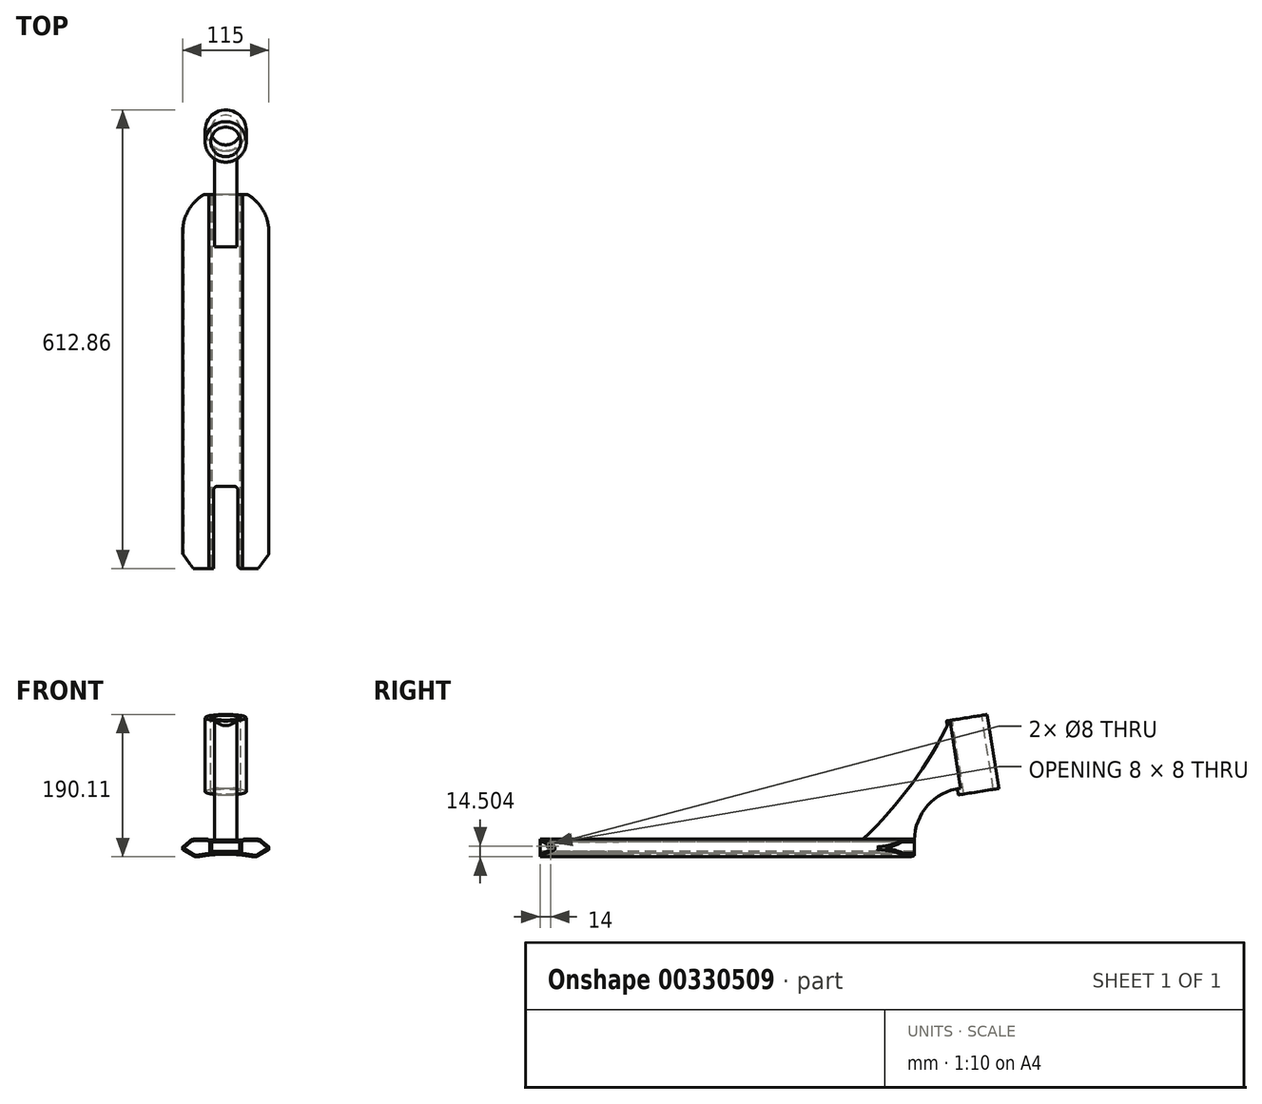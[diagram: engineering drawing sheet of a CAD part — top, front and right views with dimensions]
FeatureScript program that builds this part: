
annotation { "Feature Type Name" : "Feature", "Feature Type Description" : "" }
export const myFeature = defineFeature(function(context is Context, id is Id, definition is map)
    precondition{}
    {
        {
            var Q0;
            Q0=qCreatedBy(makeId("Front.planeOp"),FACE);
            var sketch = newSketch(context, id + "F0", { "sketchPlane" : qUnion([Q0])});
            skLineSegment(sketch, "E0", {"start": v(0, 0) * mm, "end": v(0, 27.74) * mm, "construction": true});
            skLineSegment(sketch, "E1", {"start": v(0, 23.15) * mm, "end": v(22.5, 23.15) * mm});
            skLineSegment(sketch, "E2", {"start": v(22.5, 23.15) * mm, "end": v(22.5, 24.45) * mm});
            skLineSegment(sketch, "E3", {"start": v(22.5, 24.45) * mm, "end": v(45.58, 24.45) * mm});
            skLineSegment(sketch, "E4", {"start": v(45.58, 24.45) * mm, "end": v(57.5, 14.45) * mm});
            skLineSegment(sketch, "E5", {"start": v(57.5, 14.45) * mm, "end": v(57.5, 10.45) * mm});
            skLineSegment(sketch, "E6", {"start": v(57.5, 10.45) * mm, "end": v(40.18, 0.45) * mm});
            skLineSegment(sketch, "E7.MirrorCS", {"start": v(0, 23.15) * mm, "end": v(-22.5, 23.15) * mm});
            skLineSegment(sketch, "E8.MirrorCS", {"start": v(-22.5, 23.15) * mm, "end": v(-22.5, 24.45) * mm});
            skLineSegment(sketch, "E9.MirrorCS", {"start": v(-22.5, 24.45) * mm, "end": v(-45.58, 24.45) * mm});
            skLineSegment(sketch, "E10.MirrorCS", {"start": v(-45.58, 24.45) * mm, "end": v(-57.5, 14.45) * mm});
            skLineSegment(sketch, "E11.MirrorCS", {"start": v(-57.5, 14.45) * mm, "end": v(-57.5, 10.45) * mm});
            skLineSegment(sketch, "E12.MirrorCS", {"start": v(-57.5, 10.45) * mm, "end": v(-40.18, 0.45) * mm});
            skArc(sketch, "E13", {"start": v(40.18, 0.45) * mm, "mid": v(0, 4.53) * mm, "end": v(-40.18, 0.45) * mm});
            skSolve(sketch);
        }
        {
            var Q0;
            Q0 = qSketchRegion(id + "F0", true);
            extrude(context, id + "F1", {"entities" : qUnion([Q0]), "endBound" : BoundingType.SYMMETRIC, "depth" : 500 * mm});
        }
        {
            var Q0;
            Q0=qCreatedBy(makeId("Front.planeOp"),FACE);
            var sketch = newSketch(context, id + "F2", { "sketchPlane" : qUnion([Q0])});
            skLineSegment(sketch, "E14.bottom", {"start": v(-19, 21.15) * mm, "end": v(19, 21.15) * mm});
            skLineSegment(sketch, "E14.top", {"start": v(-19, 8.15) * mm, "end": v(19, 8.15) * mm});
            skLineSegment(sketch, "E14.left", {"start": v(-19, 21.15) * mm, "end": v(-19, 8.15) * mm});
            skLineSegment(sketch, "E14.right", {"start": v(19, 21.15) * mm, "end": v(19, 8.15) * mm});
            skSolve(sketch);
        }
        {
            var Q0;
            Q0 = qSketchRegion(id + "F2", true);
            extrude(context, id + "F3", {"entities" : qUnion([Q0]), "operationType" : NewBodyOperationType.REMOVE, "endBound" : BoundingType.SYMMETRIC, "oppositeDirection" : true, "depth" : 500 * mm});
        }
        {
            var Q0;
            Q0=makeQuery(id+"F1.opExtrude","SWEPT_EDGE",EDGE,{"disambiguationData":[OSD([sQuery(id+"F0.wireOp",EDGE,"E8.MirrorCS"),sQuery(id+"F0.wireOp",EDGE,"E9.MirrorCS")])]});
            var Q1;
            Q1=makeQuery(id+"F1.opExtrude","SWEPT_EDGE",EDGE,{"disambiguationData":[OSD([sQuery(id+"F0.wireOp",EDGE,"E2"),sQuery(id+"F0.wireOp",EDGE,"E3")])]});
            fillet(context, id + "F4", {"entities" : qUnion([Q0, Q1]), "radius" : 2 * mm, "tangentPropagation" : true, "allowEdgeOverflow" : false});
        }
        {
            var Q0;
            Q0=makeQuery(id+"F1.opExtrude","SWEPT_EDGE",EDGE,{"disambiguationData":[OSD([sQuery(id+"F0.wireOp",EDGE,"E9.MirrorCS"),sQuery(id+"F0.wireOp",EDGE,"E10.MirrorCS")])]});
            var Q1;
            Q1=makeQuery(id+"F1.opExtrude","SWEPT_EDGE",EDGE,{"disambiguationData":[OSD([sQuery(id+"F0.wireOp",EDGE,"E12.MirrorCS"),sQuery(id+"F0.wireOp",EDGE,"E13")])]});
            var Q2;
            Q2=makeQuery(id+"F1.opExtrude","SWEPT_EDGE",EDGE,{"disambiguationData":[OSD([sQuery(id+"F0.wireOp",EDGE,"E6"),sQuery(id+"F0.wireOp",EDGE,"E13")])]});
            var Q3;
            Q3=makeQuery(id+"F1.opExtrude","SWEPT_EDGE",EDGE,{"disambiguationData":[OSD([sQuery(id+"F0.wireOp",EDGE,"E3"),sQuery(id+"F0.wireOp",EDGE,"E4")])]});
            fillet(context, id + "F5", {"entities" : qUnion([Q0, Q1, Q2, Q3]), "radius" : 9 * mm, "tangentPropagation" : true, "allowEdgeOverflow" : false});
        }
        {
            var Q0;
            Q0=makeQuery(id+"F1.opExtrude","SWEPT_EDGE",EDGE,{"disambiguationData":[OSD([sQuery(id+"F0.wireOp",EDGE,"E4"),sQuery(id+"F0.wireOp",EDGE,"E5")])]});
            var Q1;
            Q1=makeQuery(id+"F1.opExtrude","SWEPT_EDGE",EDGE,{"disambiguationData":[OSD([sQuery(id+"F0.wireOp",EDGE,"E5"),sQuery(id+"F0.wireOp",EDGE,"E6")])]});
            var Q2;
            Q2=makeQuery(id+"F1.opExtrude","SWEPT_EDGE",EDGE,{"disambiguationData":[OSD([sQuery(id+"F0.wireOp",EDGE,"E11.MirrorCS"),sQuery(id+"F0.wireOp",EDGE,"E12.MirrorCS")])]});
            var Q3;
            Q3=makeQuery(id+"F1.opExtrude","SWEPT_EDGE",EDGE,{"disambiguationData":[OSD([sQuery(id+"F0.wireOp",EDGE,"E10.MirrorCS"),sQuery(id+"F0.wireOp",EDGE,"E11.MirrorCS")])]});
            fillet(context, id + "F6", {"entities" : qUnion([Q0, Q1, Q2, Q3]), "radius" : 1 * mm, "tangentPropagation" : true, "allowEdgeOverflow" : false});
        }
        {
            var Q0;
            Q0=makeQuery(id+"F1.opExtrude","CAP_FACE",FACE,{"disambiguationData":[OSD([sQuery(id+"F0.wireOp",EDGE,"E1"),sQuery(id+"F0.wireOp",EDGE,"E2"),sQuery(id+"F0.wireOp",EDGE,"E3"),sQuery(id+"F0.wireOp",EDGE,"E4"),sQuery(id+"F0.wireOp",EDGE,"E5"),sQuery(id+"F0.wireOp",EDGE,"E6"),sQuery(id+"F0.wireOp",EDGE,"E7.MirrorCS"),sQuery(id+"F0.wireOp",EDGE,"E8.MirrorCS"),sQuery(id+"F0.wireOp",EDGE,"E9.MirrorCS"),sQuery(id+"F0.wireOp",EDGE,"E10.MirrorCS"),sQuery(id+"F0.wireOp",EDGE,"E11.MirrorCS"),sQuery(id+"F0.wireOp",EDGE,"E12.MirrorCS"),sQuery(id+"F0.wireOp",EDGE,"E13")])],"isStart":false});
            var sketch = newSketch(context, id + "F7", { "sketchPlane" : qUnion([Q0])});
            skLineSegment(sketch, "E15.0.0", {"start": v(43.1, 2.14) * mm, "end": v(57, 10.16) * mm});
            skArc(sketch, "E15.0.1", {"start": v(57, 10.16) * mm, "mid": v(57.37, 10.53) * mm, "end": v(57.5, 11.03) * mm});
            skLineSegment(sketch, "E15.0.2", {"start": v(57.5, 11.03) * mm, "end": v(57.5, 13.99) * mm});
            skArc(sketch, "E15.0.3", {"start": v(57.5, 13.99) * mm, "mid": v(57.4, 14.4) * mm, "end": v(57.14, 14.75) * mm});
            skLineSegment(sketch, "E15.0.4", {"start": v(57.14, 14.75) * mm, "end": v(48.1, 22.35) * mm});
            skArc(sketch, "E15.0.5", {"start": v(48.1, 22.35) * mm, "mid": v(45.38, 23.9) * mm, "end": v(42.3, 24.45) * mm});
            skLineSegment(sketch, "E15.0.6", {"start": v(42.3, 24.45) * mm, "end": v(24.37, 24.45) * mm});
            skArc(sketch, "E15.0.7", {"start": v(24.37, 24.45) * mm, "mid": v(23.23, 24.1) * mm, "end": v(22.5, 23.15) * mm});
            skLineSegment(sketch, "E15.0.8", {"start": v(22.5, 23.15) * mm, "end": v(-22.5, 23.15) * mm});
            skArc(sketch, "E15.0.9", {"start": v(-22.5, 23.15) * mm, "mid": v(-23.23, 24.1) * mm, "end": v(-24.37, 24.45) * mm});
            skLineSegment(sketch, "E15.0.10", {"start": v(-24.37, 24.45) * mm, "end": v(-42.3, 24.45) * mm});
            skArc(sketch, "E15.0.11", {"start": v(-42.3, 24.45) * mm, "mid": v(-45.38, 23.9) * mm, "end": v(-48.1, 22.35) * mm});
            skLineSegment(sketch, "E15.0.12", {"start": v(-48.1, 22.35) * mm, "end": v(-57.14, 14.75) * mm});
            skArc(sketch, "E15.0.13", {"start": v(-57.14, 14.75) * mm, "mid": v(-57.4, 14.4) * mm, "end": v(-57.5, 13.99) * mm});
            skLineSegment(sketch, "E15.0.14", {"start": v(-57.5, 13.99) * mm, "end": v(-57.5, 11.03) * mm});
            skArc(sketch, "E15.0.15", {"start": v(-57.5, 11.03) * mm, "mid": v(-57.37, 10.53) * mm, "end": v(-57, 10.16) * mm});
            skLineSegment(sketch, "E15.0.16", {"start": v(-57, 10.16) * mm, "end": v(-43.1, 2.14) * mm});
            skArc(sketch, "E15.0.17", {"start": v(-43.1, 2.14) * mm, "mid": v(-40.12, 1.06) * mm, "end": v(-36.94, 1.09) * mm});
            skArc(sketch, "E15.0.18", {"start": v(-36.94, 1.09) * mm, "mid": v(0, 4.53) * mm, "end": v(36.94, 1.09) * mm});
            skArc(sketch, "E15.0.19", {"start": v(36.94, 1.09) * mm, "mid": v(40.12, 1.06) * mm, "end": v(43.1, 2.14) * mm});
            skArc(sketch, "E16.0", {"start": v(-37.3, 3.05) * mm, "mid": v(0, 6.53) * mm, "end": v(37.3, 3.05) * mm});
            skArc(sketch, "E16.1", {"start": v(-42.1, 3.87) * mm, "mid": v(-39.78, 3.03) * mm, "end": v(-37.3, 3.05) * mm});
            skLineSegment(sketch, "E16.2", {"start": v(-24.37, 22.45) * mm, "end": v(-42.3, 22.45) * mm});
            skArc(sketch, "E16.3", {"start": v(-42.3, 22.45) * mm, "mid": v(-44.7, 22.03) * mm, "end": v(-46.8, 20.81) * mm});
            skLineSegment(sketch, "E16.4", {"start": v(-46.8, 20.81) * mm, "end": v(-55.76, 13.3) * mm});
            skLineSegment(sketch, "E16.5", {"start": v(-55.61, 11.67) * mm, "end": v(-42.1, 3.87) * mm});
            skPoint(sketch, "E17.visualSharp", {"position": v(-56.85, 12.39) * mm});
            skArc(sketch, "E17.filletArc", {"start": v(-55.76, 13.3) * mm, "mid": v(-56.1, 12.45) * mm, "end": v(-55.61, 11.67) * mm});
            skLineSegment(sketch, "E18", {"start": v(-21, 5.43) * mm, "end": v(-21, 21.15) * mm});
            skLineSegment(sketch, "E19", {"start": v(-21, 21.15) * mm, "end": v(-22.5, 21.15) * mm});
            skArc(sketch, "E20", {"start": v(-22.5, 21.15) * mm, "mid": v(-23.23, 22.1) * mm, "end": v(-24.37, 22.45) * mm});
            skLineSegment(sketch, "E21.MirrorCS", {"start": v(21, 5.43) * mm, "end": v(21, 21.15) * mm});
            skLineSegment(sketch, "E22.MirrorCS", {"start": v(21, 21.15) * mm, "end": v(22.5, 21.15) * mm});
            skArc(sketch, "E23.MirrorCS", {"start": v(22.5, 21.15) * mm, "mid": v(23.23, 22.1) * mm, "end": v(24.37, 22.45) * mm});
            skLineSegment(sketch, "E24.MirrorCS", {"start": v(24.37, 22.45) * mm, "end": v(42.3, 22.45) * mm});
            skArc(sketch, "E25.MirrorCS", {"start": v(42.3, 22.45) * mm, "mid": v(44.7, 22.03) * mm, "end": v(46.8, 20.81) * mm});
            skLineSegment(sketch, "E26.MirrorCS", {"start": v(46.8, 20.81) * mm, "end": v(55.76, 13.3) * mm});
            skArc(sketch, "E27.MirrorCS", {"start": v(55.76, 13.3) * mm, "mid": v(56.1, 12.45) * mm, "end": v(55.61, 11.67) * mm});
            skLineSegment(sketch, "E28.MirrorCS", {"start": v(55.61, 11.67) * mm, "end": v(42.1, 3.87) * mm});
            skArc(sketch, "E29.MirrorCS", {"start": v(42.1, 3.87) * mm, "mid": v(39.78, 3.03) * mm, "end": v(37.3, 3.05) * mm});
            skArc(sketch, "E30.MirrorCS", {"start": v(37.3, 3.05) * mm, "mid": v(0, 6.53) * mm, "end": v(-37.3, 3.05) * mm});
            skSolve(sketch);
        }
        {
            var Q0;
            {var subQ0=sQuery(id+"F7.wireOp",EDGE,"E16.1");Q0=makeQuery(id+"F7.imprint","IMPRINT",FACE,{"disambiguationData":[TD([[makeQuery(id+"F7.imprint","IMPRINT",EDGE,{"derivedFrom":subQ0}),1.0]])]});}
            var Q1;
            {var subQ0=sQuery(id+"F7.wireOp",EDGE,"E21.MirrorCS");Q1=makeQuery(id+"F7.imprint","IMPRINT",FACE,{"disambiguationData":[TD([[makeQuery(id+"F7.imprint","IMPRINT",EDGE,{"derivedFrom":subQ0}),-1.0]])]});}
            extrude(context, id + "F8", {"entities" : qUnion([Q0, Q1]), "operationType" : NewBodyOperationType.REMOVE, "endBound" : BoundingType.THROUGH_ALL, "oppositeDirection" : true, "depth" : 25 * mm});
        }
        {
            var Q0;
            Q0=qCreatedBy(makeId("Top.planeOp"),FACE);
            var sketch = newSketch(context, id + "F9", { "sketchPlane" : qUnion([Q0])});
            skArc(sketch, "E31", {"start": v(57.5, 200) * mm, "mid": v(0, 257.5) * mm, "end": v(-57.5, 200) * mm});
            skLineSegment(sketch, "E32", {"start": v(57.5, 200) * mm, "end": v(57.5, 280) * mm});
            skLineSegment(sketch, "E33", {"start": v(57.5, 280) * mm, "end": v(-57.5, 280) * mm});
            skLineSegment(sketch, "E34", {"start": v(-57.5, 280) * mm, "end": v(-57.5, 200) * mm});
            skSolve(sketch);
        }
        {
            var Q0;
            Q0 = qSketchRegion(id + "F9", true);
            extrude(context, id + "F10", {"entities" : qUnion([Q0]), "operationType" : NewBodyOperationType.REMOVE, "endBound" : BoundingType.THROUGH_ALL, "depth" : 25 * mm, "hasSecondDirection" : true, "secondDirectionBound" : SecondDirectionBoundingType.THROUGH_ALL, "secondDirectionOppositeDirection" : true, "secondDirectionDepth" : 25 * mm});
        }
        {
            var Q0;
            Q0=qCreatedBy(makeId("Top.planeOp"),FACE);
            var sketch = newSketch(context, id + "F11", { "sketchPlane" : qUnion([Q0])});
            skLineSegment(sketch, "E35", {"start": v(-68, -216) * mm, "end": v(-43.3, -250) * mm});
            skLineSegment(sketch, "E36", {"start": v(-68, -216) * mm, "end": v(-68, -346) * mm});
            skLineSegment(sketch, "E37", {"start": v(-68, -346) * mm, "end": v(68, -346) * mm});
            skLineSegment(sketch, "E38", {"start": v(68, -346) * mm, "end": v(68, -216) * mm});
            skLineSegment(sketch, "E39", {"start": v(68, -216) * mm, "end": v(43.3, -250) * mm});
            skLineSegment(sketch, "E40", {"start": v(-43.3, -250) * mm, "end": v(-16, -250) * mm});
            skLineSegment(sketch, "E41", {"start": v(-16, -250) * mm, "end": v(-16, -140) * mm});
            skLineSegment(sketch, "E42", {"start": v(-16, -140) * mm, "end": v(16, -140) * mm});
            skLineSegment(sketch, "E43", {"start": v(16, -140) * mm, "end": v(16, -250) * mm});
            skLineSegment(sketch, "E44", {"start": v(16, -250) * mm, "end": v(43.3, -250) * mm});
            skSolve(sketch);
        }
        {
            var Q0;
            Q0 = qSketchRegion(id + "F11", true);
            extrude(context, id + "F12", {"entities" : qUnion([Q0]), "operationType" : NewBodyOperationType.REMOVE, "endBound" : BoundingType.THROUGH_ALL, "oppositeDirection" : true, "depth" : 25 * mm, "hasSecondDirection" : true, "secondDirectionBound" : SecondDirectionBoundingType.THROUGH_ALL, "secondDirectionOppositeDirection" : false, "secondDirectionDepth" : 25 * mm});
        }
        {
            var Q0;
            {var subQ2=sQuery(id+"F11.wireOp",EDGE,"E43");Q0=makeQuery(id+"F12.boolean.opBoolean","COPY",EDGE,{"disambiguationData":[TD([makeQuery(id+"F3.boolean.opBoolean","COPY",FACE,{"derivedFrom":makeQuery(id+"F3.opExtrude","SWEPT_FACE",FACE,{"disambiguationData":[OSD([sQuery(id+"F2.wireOp",EDGE,"E14.bottom")])]})})])],"derivedFrom":makeQuery(id+"F12.opExtrude","SWEPT_EDGE",EDGE,{"disambiguationData":[OSD([subQ2,sQuery(id+"F11.wireOp",EDGE,"E44")])]})});}
            var Q1;
            {var subQ0=sQuery(id+"F0.wireOp",EDGE,"E13");var subQ1=sQuery(id+"F11.wireOp",EDGE,"E43");Q1=makeQuery(id+"F12.boolean.opBoolean","COPY",EDGE,{"disambiguationData":[TD([makeQuery(id+"F1.opExtrude","SWEPT_FACE",FACE,{"disambiguationData":[OSD([subQ0])]})])],"derivedFrom":makeQuery(id+"F12.opExtrude","SWEPT_EDGE",EDGE,{"disambiguationData":[OSD([subQ1,sQuery(id+"F11.wireOp",EDGE,"E44")])]})});}
            var Q2;
            {var subQ0=sQuery(id+"F11.wireOp",EDGE,"E42");var subQ1=sQuery(id+"F11.wireOp",EDGE,"E43");Q2=makeQuery(id+"F12.boolean.opBoolean","COPY",EDGE,{"disambiguationData":[TD([makeQuery(id+"F3.boolean.opBoolean","COPY",FACE,{"derivedFrom":makeQuery(id+"F3.opExtrude","SWEPT_FACE",FACE,{"disambiguationData":[OSD([sQuery(id+"F2.wireOp",EDGE,"E14.bottom")])]})})])],"derivedFrom":makeQuery(id+"F12.opExtrude","SWEPT_EDGE",EDGE,{"disambiguationData":[OSD([subQ0,subQ1])]})});}
            var Q3;
            {var subQ0=sQuery(id+"F11.wireOp",EDGE,"E43");var subQ1=sQuery(id+"F11.wireOp",EDGE,"E42");Q3=makeQuery(id+"F12.boolean.opBoolean","COPY",EDGE,{"disambiguationData":[TD([makeQuery(id+"F1.opExtrude","SWEPT_FACE",FACE,{"disambiguationData":[OSD([sQuery(id+"F0.wireOp",EDGE,"E13")])]})])],"derivedFrom":makeQuery(id+"F12.opExtrude","SWEPT_EDGE",EDGE,{"disambiguationData":[OSD([subQ1,subQ0])]})});}
            var Q4;
            {var subQ0=sQuery(id+"F11.wireOp",EDGE,"E42");var subQ1=sQuery(id+"F11.wireOp",EDGE,"E41");Q4=makeQuery(id+"F12.boolean.opBoolean","COPY",EDGE,{"disambiguationData":[TD([makeQuery(id+"F3.boolean.opBoolean","COPY",FACE,{"derivedFrom":makeQuery(id+"F3.opExtrude","SWEPT_FACE",FACE,{"disambiguationData":[OSD([sQuery(id+"F2.wireOp",EDGE,"E14.bottom")])]})})])],"derivedFrom":makeQuery(id+"F12.opExtrude","SWEPT_EDGE",EDGE,{"disambiguationData":[OSD([subQ1,subQ0])]})});}
            var Q5;
            {var subQ0=sQuery(id+"F11.wireOp",EDGE,"E41");var subQ1=sQuery(id+"F11.wireOp",EDGE,"E42");Q5=makeQuery(id+"F12.boolean.opBoolean","COPY",EDGE,{"disambiguationData":[TD([makeQuery(id+"F1.opExtrude","SWEPT_FACE",FACE,{"disambiguationData":[OSD([sQuery(id+"F0.wireOp",EDGE,"E13")])]})])],"derivedFrom":makeQuery(id+"F12.opExtrude","SWEPT_EDGE",EDGE,{"disambiguationData":[OSD([subQ0,subQ1])]})});}
            var Q6;
            {var subQ2=sQuery(id+"F11.wireOp",EDGE,"E41");Q6=makeQuery(id+"F12.boolean.opBoolean","COPY",EDGE,{"disambiguationData":[TD([makeQuery(id+"F3.boolean.opBoolean","COPY",FACE,{"derivedFrom":makeQuery(id+"F3.opExtrude","SWEPT_FACE",FACE,{"disambiguationData":[OSD([sQuery(id+"F2.wireOp",EDGE,"E14.bottom")])]})})])],"derivedFrom":makeQuery(id+"F12.opExtrude","SWEPT_EDGE",EDGE,{"disambiguationData":[OSD([sQuery(id+"F11.wireOp",EDGE,"E40"),subQ2])]})});}
            var Q7;
            {var subQ0=sQuery(id+"F0.wireOp",EDGE,"E13");var subQ1=sQuery(id+"F11.wireOp",EDGE,"E41");Q7=makeQuery(id+"F12.boolean.opBoolean","COPY",EDGE,{"disambiguationData":[TD([makeQuery(id+"F1.opExtrude","SWEPT_FACE",FACE,{"disambiguationData":[OSD([subQ0])]})])],"derivedFrom":makeQuery(id+"F12.opExtrude","SWEPT_EDGE",EDGE,{"disambiguationData":[OSD([sQuery(id+"F11.wireOp",EDGE,"E40"),subQ1])]})});}
            fillet(context, id + "F13", {"entities" : qUnion([Q0, Q1, Q2, Q3, Q4, Q5, Q6, Q7]), "radius" : 5 * mm, "tangentPropagation" : true, "allowEdgeOverflow" : false});
        }
        {
            var Q0;
            Q0=qCreatedBy(makeId("Right.planeOp"),FACE);
            var sketch = newSketch(context, id + "F14", { "sketchPlane" : qUnion([Q0])});
            skLineSegment(sketch, "E45", {"start": v(180, 23.15) * mm, "end": v(250, 23.15) * mm});
            skArc(sketch, "E46", {"start": v(311.71, 92.66) * mm, "mid": v(267.66, 69.63) * mm, "end": v(250, 23.15) * mm});
            skLineSegment(sketch, "E47", {"start": v(313.03, 84.38) * mm, "end": v(358.46, 91.58) * mm});
            skLineSegment(sketch, "E48", {"start": v(358.46, 91.58) * mm, "end": v(342.82, 190.35) * mm});
            skLineSegment(sketch, "E49", {"start": v(342.82, 190.35) * mm, "end": v(297.38, 183.15) * mm});
            skArc(sketch, "E50", {"start": v(180, 23.15) * mm, "mid": v(245.97, 97.81) * mm, "end": v(297.38, 183.15) * mm});
            skLineSegment(sketch, "E51", {"start": v(311.71, 92.66) * mm, "end": v(313.03, 84.38) * mm});
            skSolve(sketch);
        }
        {
            var Q0;
            Q0 = qSketchRegion(id + "F14", true);
            extrude(context, id + "F15", {"entities" : qUnion([Q0]), "operationType" : NewBodyOperationType.ADD, "endBound" : BoundingType.SYMMETRIC, "depth" : 30 * mm});
        }
        {
            var Q0;
            Q0=makeQuery(id+"F15.opExtrude","SWEPT_FACE",FACE,{"disambiguationData":[OSD([sQuery(id+"F14.wireOp",EDGE,"E49")])]});
            var sketch = newSketch(context, id + "F16", { "sketchPlane" : qUnion([Q0])});
            skCircle(sketch, "E52", {"center": v(0, 345.37) * mm, "radius": 27.46 * mm});
            skSolve(sketch);
        }
        {
            var Q0;
            Q0 = qSketchRegion(id + "F16", true);
            var Q1;
            Q1=makeQuery(id+"F15.opExtrude","SWEPT_FACE",FACE,{"disambiguationData":[OSD([sQuery(id+"F14.wireOp",EDGE,"E47")])]});
            extrude(context, id + "F17", {"entities" : qUnion([Q0]), "operationType" : NewBodyOperationType.ADD, "endBound" : BoundingType.UP_TO_SURFACE, "oppositeDirection" : true, "endBoundEntityFace" : qUnion([Q1]), "depth" : 25 * mm});
        }
        {
            var Q0;
            Q0=makeQuery(id+"F17.boolean.opBoolean","MERGE",FACE,{"derivedFrom":[makeQuery(id+"F15.opExtrude","SWEPT_FACE",FACE,{"disambiguationData":[OSD([sQuery(id+"F14.wireOp",EDGE,"E49")])]}),makeQuery(id+"F17.opExtrude","CAP_FACE",FACE,{"disambiguationData":[OSD([sQuery(id+"F16.wireOp",EDGE,"E52")])],"isStart":true})]});
            var sketch = newSketch(context, id + "F18", { "sketchPlane" : qUnion([Q0])});
            skPoint(sketch, "E53", {"position": v(0, 345.37) * mm});
            skSolve(sketch);
        }
        {
            var Q0;
            Q0=sQuery(id+"F18.wireOp",VERTEX,"E53");
            var Q1;
            Q1=makeQuery(id+"F1.opExtrude","SWEPT_BODY",BODY,{"disambiguationData":[OSD([sQuery(id+"F0.wireOp",EDGE,"E1"),sQuery(id+"F0.wireOp",EDGE,"E2"),sQuery(id+"F0.wireOp",EDGE,"E3"),sQuery(id+"F0.wireOp",EDGE,"E4"),sQuery(id+"F0.wireOp",EDGE,"E5"),sQuery(id+"F0.wireOp",EDGE,"E6"),sQuery(id+"F0.wireOp",EDGE,"E7.MirrorCS"),sQuery(id+"F0.wireOp",EDGE,"E8.MirrorCS"),sQuery(id+"F0.wireOp",EDGE,"E9.MirrorCS"),sQuery(id+"F0.wireOp",EDGE,"E10.MirrorCS"),sQuery(id+"F0.wireOp",EDGE,"E11.MirrorCS"),sQuery(id+"F0.wireOp",EDGE,"E12.MirrorCS"),sQuery(id+"F0.wireOp",EDGE,"E13")])]});
            hole(context, id + "F19", {"style" : HoleStyle.SIMPLE, "endStyle" : HoleEndStyle.THROUGH, "holeDiameter" : 40 * mm, "isTappedThrough" : true, "tappedDepth" : 12 * mm, "tapClearance" : 3, "locations" : qUnion([Q0]), "scope" : qUnion([Q1])});
        }
        {
            var Q0;
            Q0=makeQuery(id+"F8.boolean.opBoolean","COPY",FACE,{"derivedFrom":makeQuery(id+"F8.opExtrude","SWEPT_FACE",FACE,{"disambiguationData":[OSD([sQuery(id+"F7.wireOp",EDGE,"E21.MirrorCS")])]})});
            var sketch = newSketch(context, id + "F20", { "sketchPlane" : qUnion([Q0])});
            skPoint(sketch, "E54", {"position": v(-236, 15.43) * mm});
            skSolve(sketch);
        }
        {
            var Q0;
            Q0=sQuery(id+"F20.wireOp",VERTEX,"E54");
            var Q1;
            Q1=makeQuery(id+"F1.opExtrude","SWEPT_BODY",BODY,{"disambiguationData":[OSD([sQuery(id+"F0.wireOp",EDGE,"E1"),sQuery(id+"F0.wireOp",EDGE,"E2"),sQuery(id+"F0.wireOp",EDGE,"E3"),sQuery(id+"F0.wireOp",EDGE,"E4"),sQuery(id+"F0.wireOp",EDGE,"E5"),sQuery(id+"F0.wireOp",EDGE,"E6"),sQuery(id+"F0.wireOp",EDGE,"E7.MirrorCS"),sQuery(id+"F0.wireOp",EDGE,"E8.MirrorCS"),sQuery(id+"F0.wireOp",EDGE,"E9.MirrorCS"),sQuery(id+"F0.wireOp",EDGE,"E10.MirrorCS"),sQuery(id+"F0.wireOp",EDGE,"E11.MirrorCS"),sQuery(id+"F0.wireOp",EDGE,"E12.MirrorCS"),sQuery(id+"F0.wireOp",EDGE,"E13")])]});
            hole(context, id + "F21", {"style" : HoleStyle.SIMPLE, "endStyle" : HoleEndStyle.BLIND, "holeDiameter" : 8 * mm, "holeDepth" : 50 * mm, "isTappedThrough" : true, "tappedDepth" : 12 * mm, "tapClearance" : 3, "locations" : qUnion([Q0]), "scope" : qUnion([Q1])});
        }
    });
